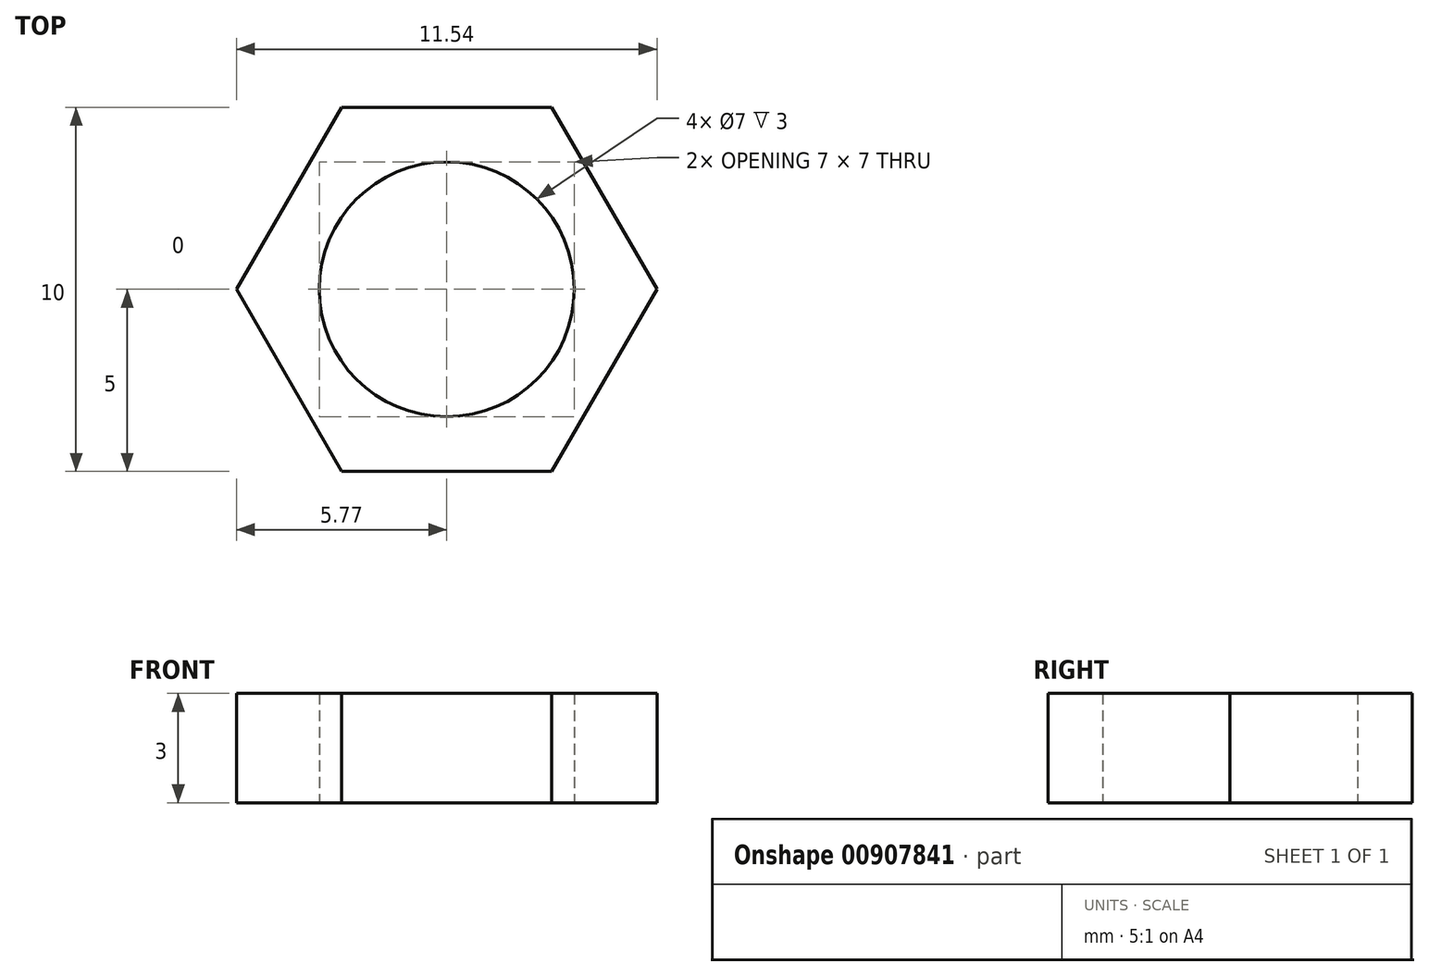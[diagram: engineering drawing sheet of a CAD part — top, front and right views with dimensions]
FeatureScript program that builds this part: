
annotation { "Feature Type Name" : "Feature", "Feature Type Description" : "" }
export const myFeature = defineFeature(function(context is Context, id is Id, definition is map)
    precondition{}
    {
        {
            var Q0;
            Q0=qCreatedBy(makeId("Top.planeOp"),FACE);
            var sketch = newSketch(context, id + "F0", { "sketchPlane" : qUnion([Q0])});
            skCircle(sketch, "E0.cCircle", {"center": v(0, 0) * mm, "radius": 5 * mm, "construction": true});
            skLineSegment(sketch, "E0.0", {"start": v(-2.89, 5) * mm, "end": v(2.89, 5) * mm});
            skLineSegment(sketch, "E0.1", {"start": v(2.89, 5) * mm, "end": v(5.77, 0) * mm});
            skLineSegment(sketch, "E0.2", {"start": v(5.77, 0) * mm, "end": v(2.89, -5) * mm});
            skLineSegment(sketch, "E0.3", {"start": v(2.89, -5) * mm, "end": v(-2.89, -5) * mm});
            skLineSegment(sketch, "E0.4", {"start": v(-2.89, -5) * mm, "end": v(-5.77, 0) * mm});
            skLineSegment(sketch, "E0.5", {"start": v(-5.77, 0) * mm, "end": v(-2.89, 5) * mm});
            skPoint(sketch, "E0.0.midPoint", {"position": v(0, 5) * mm});
            skLineSegment(sketch, "E1", {"start": v(0, 0) * mm, "end": v(0, 13.42) * mm, "construction": true});
            skSolve(sketch);
        }
        {
            var Q0;
            Q0 = qSketchRegion(id + "F0", true);
            extrude(context, id + "F1", {"entities" : qUnion([Q0]), "depth" : 3 * mm, "offsetDistance" : 25 * mm});
        }
        {
            var Q0;
            Q0=makeQuery(id+"F1.opExtrude","CAP_FACE",FACE,{"disambiguationData":[OSD([sQuery(id+"F0.wireOp",EDGE,"E0.0"),sQuery(id+"F0.wireOp",EDGE,"E0.1"),sQuery(id+"F0.wireOp",EDGE,"E0.2"),sQuery(id+"F0.wireOp",EDGE,"E0.3"),sQuery(id+"F0.wireOp",EDGE,"E0.4"),sQuery(id+"F0.wireOp",EDGE,"E0.5")])],"isStart":true});
            var sketch = newSketch(context, id + "F2", { "sketchPlane" : qUnion([Q0])});
            skPoint(sketch, "E2", {"position": v(0, 0) * mm});
            skSolve(sketch);
        }
        {
            var Q0;
            Q0=sQuery(id+"F2.wireOp",VERTEX,"E2");
            var Q1;
            Q1=makeQuery(id+"F1.opExtrude","SWEPT_BODY",BODY,{"disambiguationData":[OSD([sQuery(id+"F0.wireOp",EDGE,"E0.0"),sQuery(id+"F0.wireOp",EDGE,"E0.1"),sQuery(id+"F0.wireOp",EDGE,"E0.2"),sQuery(id+"F0.wireOp",EDGE,"E0.3"),sQuery(id+"F0.wireOp",EDGE,"E0.4"),sQuery(id+"F0.wireOp",EDGE,"E0.5")])]});
            hole(context, id + "F3", {"style" : HoleStyle.SIMPLE, "endStyle" : HoleEndStyle.THROUGH, "holeDiameter" : 7 * mm, "majorDiameter" : 5 * mm, "isTappedThrough" : true, "tappedDepth" : 12 * mm, "tapClearance" : 3, "startFromSketch" : true, "locations" : qUnion([Q0]), "scope" : qUnion([Q1])});
        }
    });
